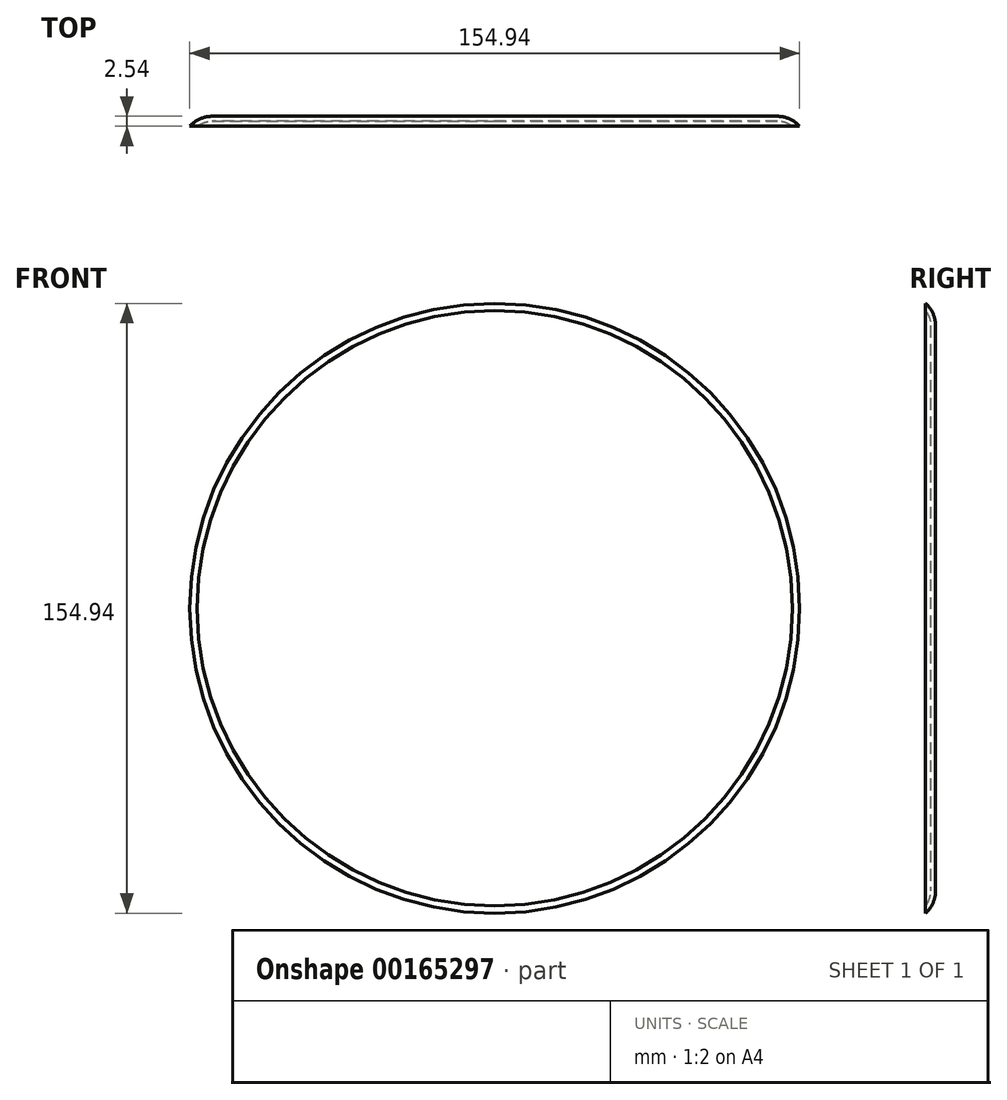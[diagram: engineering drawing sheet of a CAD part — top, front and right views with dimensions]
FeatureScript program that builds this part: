
annotation { "Feature Type Name" : "Feature", "Feature Type Description" : "" }
export const myFeature = defineFeature(function(context is Context, id is Id, definition is map)
    precondition{}
    {
        {
            var Q0;
            Q0=qCreatedBy(makeId("Front.planeOp"),FACE);
            var sketch = newSketch(context, id + "F0", { "sketchPlane" : qUnion([Q0])});
            skCircle(sketch, "E0", {"center": v(0, 0) * mm, "radius": 77.47 * mm});
            skSolve(sketch);
        }
        {
            var Q0;
            Q0 = qSketchRegion(id + "F0", true);
            extrude(context, id + "F1", {"entities" : qUnion([Q0]), "depth" : 2.54 * mm});
        }
        {
            var Q0;
            Q0=makeQuery(id+"F1.opExtrude","CAP_FACE",FACE,{"disambiguationData":[OSD([sQuery(id+"F0.wireOp",EDGE,"E0")])],"isStart":true});
            fillet(context, id + "F2", {"entities" : qUnion([Q0]), "radius" : 7.62 * mm, "tangentPropagation" : true, "allowEdgeOverflow" : false});
        }
        {
            var Q0;
            Q0=makeQuery(id+"F1.opExtrude","CAP_FACE",FACE,{"disambiguationData":[OSD([sQuery(id+"F0.wireOp",EDGE,"u3gPjoPy-e3RK-YvJ1-Y6tB-a15mpDRzR7Fs")])],"isStart":false});
            var Q1;
            Q1=makeQuery(id+"F1.opExtrude","CAP_FACE",FACE,{"disambiguationData":[OSD([sQuery(id+"F0.wireOp",EDGE,"E0")])],"isStart":false});
            shell(context, id + "F3", {"entities" : qUnion([Q0, Q1]), "thickness" : 1.27 * mm});
        }
    });
